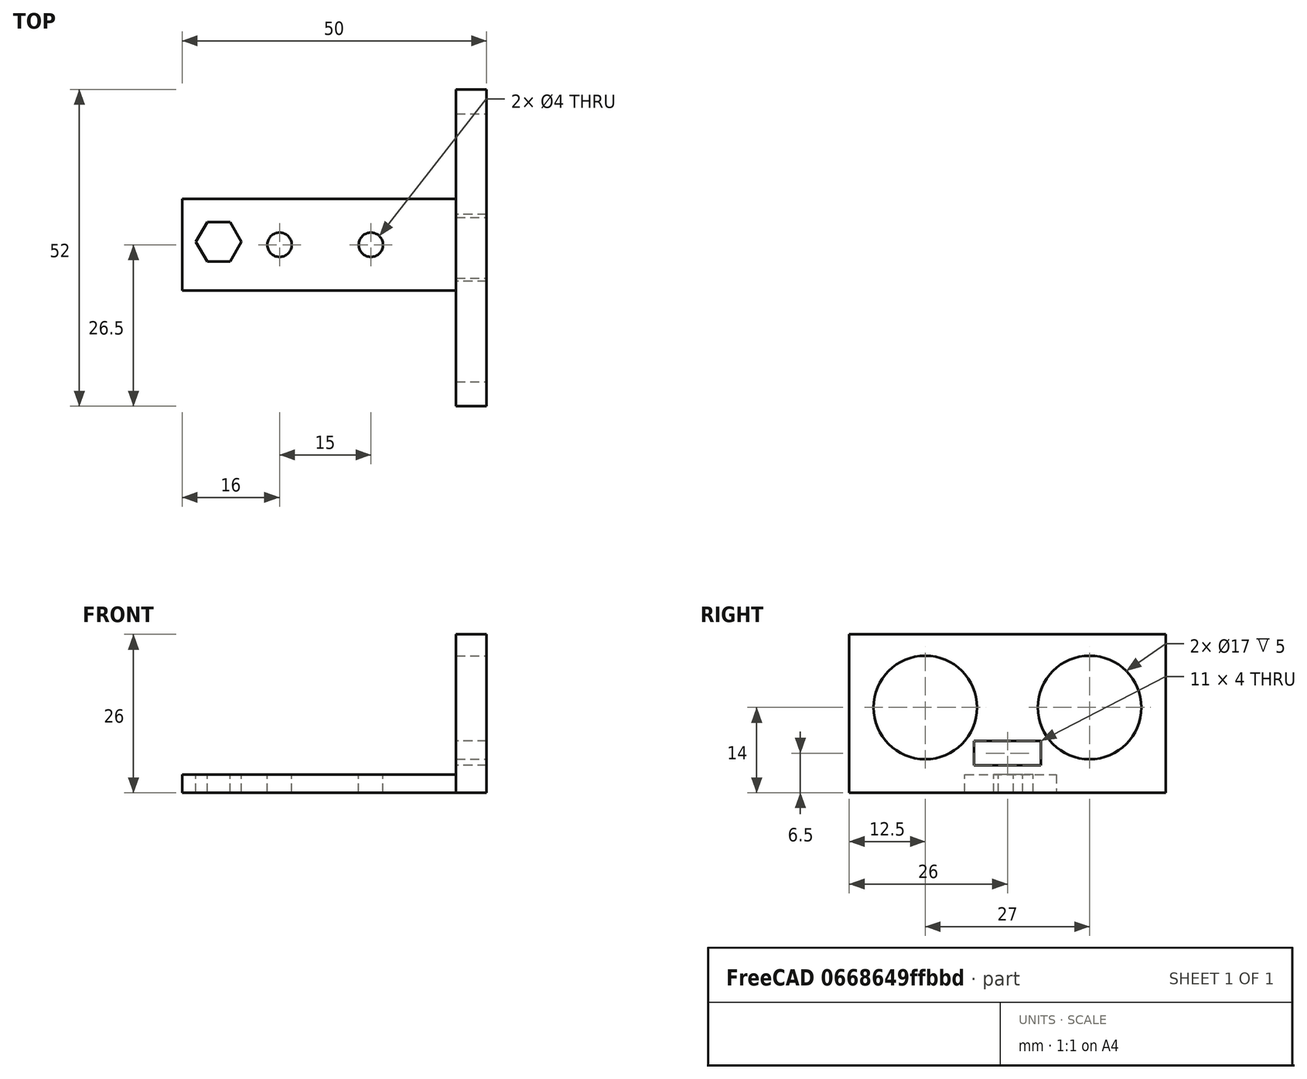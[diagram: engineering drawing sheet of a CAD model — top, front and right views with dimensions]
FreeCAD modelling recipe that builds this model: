
FCSTD DOCUMENT  (FreeCAD 0.17R13541 (Git))
Label: soporteUS
License: All rights reserved
LicenseURL: http://en.wikipedia.org/wiki/All_rights_reserved
objects: Part::Box×5, Part::Cut×5, Part::Cylinder×4, Part::MultiFuse×4, Part::Prism×1, Part::Feature×1, Mesh::Feature×1
note: 20 computed .brp shape members not serialized (recipe doc carries the construction recipe); baked Part::Feature solids carry a one-line shape summary decoded from their .brp

FEATURE [Part::Box] Box022  label="Cubo020"
  AttacherType = Attacher::AttachEngine3D
  Height = 4
  Length = 11
  Placement = pos=(15.5,-5,0.5) rot=(0,0,1;0rad)
  Width = 10
FEATURE [Part::Box] Box023  label="Cubo021"
  AttacherType = Attacher::AttachEngine3D
  Height = 10
  Length = 20
  Placement = pos=(29,5,-5) rot=(0,0,1;0rad)
  Width = 50
FEATURE [Part::Cylinder] Cylinder042  label="Cilindro042"
  Angle = 360
  AttacherType = Attacher::AttachEngine3D
  Height = 10
  Placement = pos=(7.5,6,10) rot=(1,0,0;1.5708rad)
  Radius = 8.5
FEATURE [Part::Box] Box024  label="Cubo022"
  AttacherType = Attacher::AttachEngine3D
  Height = 10
  Length = 20
  Placement = pos=(-6,5,-5) rot=(0,0,1;0rad)
  Width = 50
FEATURE [Part::MultiFuse] Fusion017
  Shapes = -> [Box024,Box023]
FEATURE [Part::Box] Box025  label="Cubo023"
  AttacherType = Attacher::AttachEngine3D
  Height = 26
  Length = 52
  Placement = pos=(-5,0,-4) rot=(0,0,1;0rad)
  Width = 5
FEATURE [Part::Box] Box026  label="Cubo024"
  AttacherType = Attacher::AttachEngine3D
  Height = 3
  Length = 52
  Placement = pos=(-5,0,-4) rot=(0,0,1;0rad)
  Width = 50
FEATURE [Part::MultiFuse] Fusion018
  Shapes = -> [Box025,Box026]
FEATURE [Part::Cylinder] Cylinder043  label="Cilindro043"
  Angle = 360
  AttacherType = Attacher::AttachEngine3D
  Height = 10
  Placement = pos=(34.5,6,10) rot=(1,0,0;1.5708rad)
  Radius = 8.5
FEATURE [Part::MultiFuse] Fusion019
  Shapes = -> [Cylinder042,Cylinder043]
FEATURE [Part::MultiFuse] Fusion016
  Shapes = -> [Box022,Fusion019]
FEATURE [Part::Cut] Cut032
  Base = -> Fusion018
  Tool = -> Fusion016
FEATURE [Part::Cylinder] Cylinder041  label="Cilindro041"
  Angle = 360
  AttacherType = Attacher::AttachEngine3D
  Height = 10
  Placement = pos=(21.5,34,-9) rot=(0,0,1;0rad)
  Radius = 2
FEATURE [Part::Cylinder] Cylinder044  label="Cilindro044"
  Angle = 360
  AttacherType = Attacher::AttachEngine3D
  Height = 10
  Placement = pos=(21.5,19,-9) rot=(0,0,1;0rad)
  Radius = 2
FEATURE [Part::Cut] Cut034
  Base = -> Cut032
  Tool = -> Cylinder041
FEATURE [Part::Cut] Cut035
  Base = -> Cut034
  Tool = -> Fusion017
FEATURE [Part::Cut] Cut033
  Base = -> Cut035
  Placement = pos=(184,-18,8) rot=(0,0,1;1.5708rad)
  Tool = -> Cylinder044
FEATURE [Part::Prism] Prism015  label="Prisma015"
  AttacherType = Attacher::AttachEngine3D
  Circumradius = 3.75
  Height = 12
  Placement = pos=(140,4,0) rot=(0,0,1;0rad)
  Polygon = 6
FEATURE [Part::Cut] Cut036  label="SOPORTEUS"
  Base = -> Cut033
  Placement = pos=(-42,-4,0) rot=(0,0,1;0rad)
  Tool = -> Prism015
FEATURE [Part::Feature] Cut036_solid  label="SOPORTEUS (Solid)"
  shape: bbox 50 x 52 x 26 mm, 32 faces (baked)
FEATURE [Mesh::Feature] Mesh  label="SOPORTEUS (Solid) (Meshed)"
